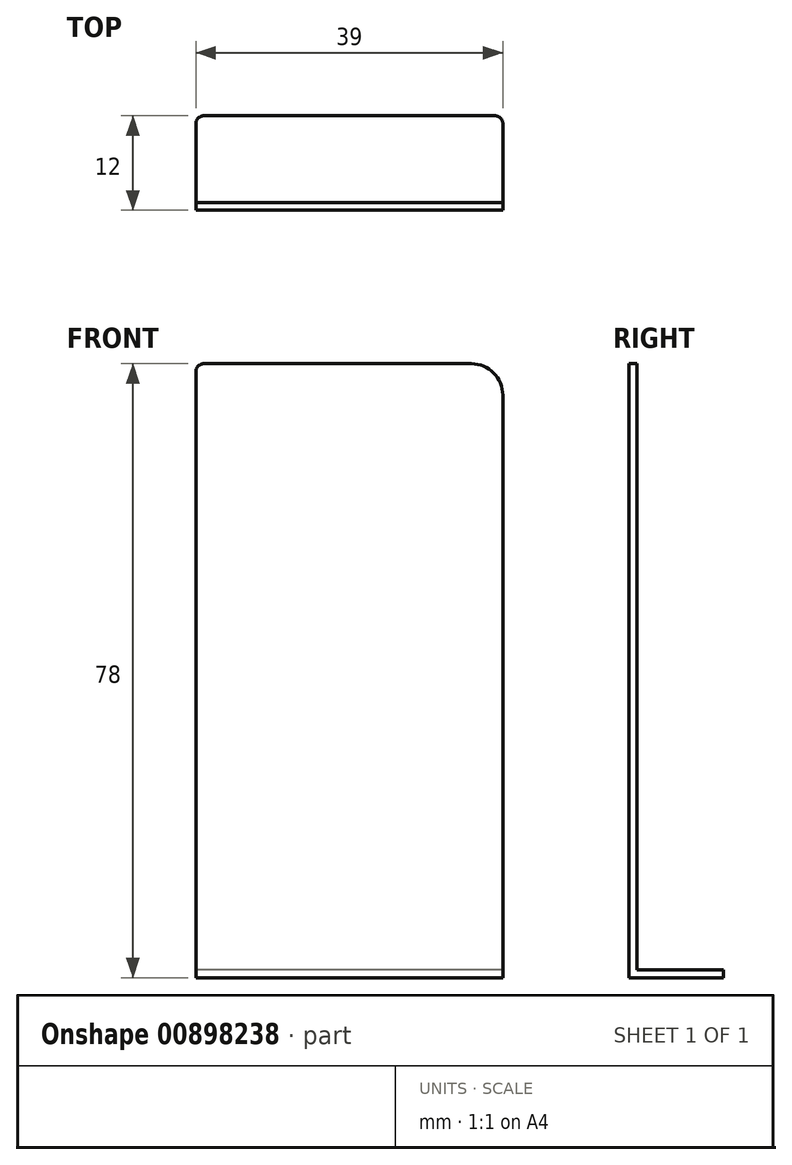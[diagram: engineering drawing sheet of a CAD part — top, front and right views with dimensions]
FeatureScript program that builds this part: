
annotation { "Feature Type Name" : "Feature", "Feature Type Description" : "" }
export const myFeature = defineFeature(function(context is Context, id is Id, definition is map)
    precondition{}
    {
        {
            var Q0;
            Q0=qCreatedBy(makeId("Right.planeOp"),FACE);
            var sketch = newSketch(context, id + "F0", { "sketchPlane" : qUnion([Q0])});
            skLineSegment(sketch, "E0", {"start": v(0, 0) * mm, "end": v(0, 78) * mm});
            skLineSegment(sketch, "E1", {"start": v(0, 78) * mm, "end": v(1, 78) * mm});
            skLineSegment(sketch, "E2", {"start": v(1, 78) * mm, "end": v(1, 1) * mm});
            skLineSegment(sketch, "E3", {"start": v(1, 1) * mm, "end": v(12, 1) * mm});
            skLineSegment(sketch, "E4", {"start": v(12, 1) * mm, "end": v(12, 0) * mm});
            skLineSegment(sketch, "E5", {"start": v(12, 0) * mm, "end": v(0, 0) * mm});
            skSolve(sketch);
        }
        {
            var Q0;
            Q0=qSketchRegion(id+"F0",true);
            extrude(context, id + "F1", {"entities" : qUnion([Q0]), "depth" : 39 * mm});
        }
        {
            var Q0;
            Q0=makeQuery(id+"F1.opExtrude","CAP_EDGE",EDGE,{"disambiguationData":[OSD([sQuery(id+"F0.wireOp",EDGE,"E1")])],"isStart":false});
            fillet(context, id + "F2", {"entities" : qUnion([Q0]), "radius" : 4 * mm, "tangentPropagation" : true, "allowEdgeOverflow" : false});
        }
        {
            var Q0;
            Q0=makeQuery(id+"F1.opExtrude","CAP_EDGE",EDGE,{"disambiguationData":[OSD([sQuery(id+"F0.wireOp",EDGE,"E1")])],"isStart":true});
            var Q1;
            Q1=makeQuery(id+"F1.opExtrude","CAP_EDGE",EDGE,{"disambiguationData":[OSD([sQuery(id+"F0.wireOp",EDGE,"E4")])],"isStart":false});
            var Q2;
            Q2=makeQuery(id+"F1.opExtrude","CAP_EDGE",EDGE,{"disambiguationData":[OSD([sQuery(id+"F0.wireOp",EDGE,"E4")])],"isStart":true});
            fillet(context, id + "F3", {"entities" : qUnion([Q0, Q1, Q2]), "radius" : 1 * mm, "tangentPropagation" : true, "allowEdgeOverflow" : false});
        }
    });
